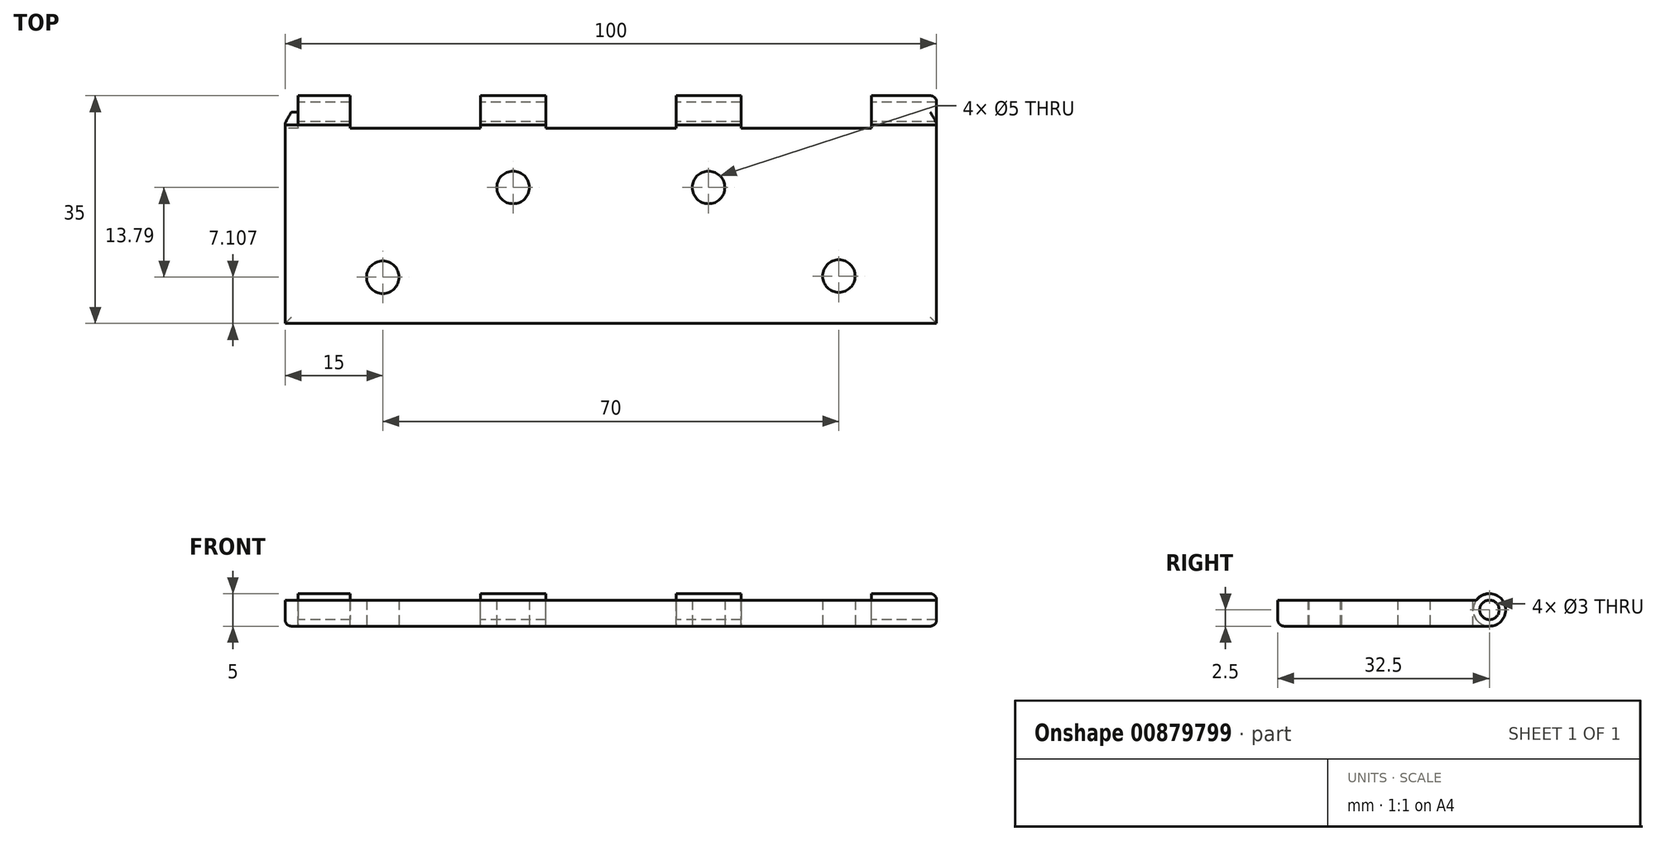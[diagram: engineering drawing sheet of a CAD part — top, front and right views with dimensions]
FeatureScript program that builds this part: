
annotation { "Feature Type Name" : "Feature", "Feature Type Description" : "" }
export const myFeature = defineFeature(function(context is Context, id is Id, definition is map)
    precondition{}
    {
        {
            var Q0;
            Q0=qCreatedBy(makeId("Top.planeOp"),FACE);
            var sketch = newSketch(context, id + "F0", { "sketchPlane" : qUnion([Q0])});
            skLineSegment(sketch, "E0.bottom", {"start": v(-50, 15) * mm, "end": v(50, 15) * mm});
            skLineSegment(sketch, "E0.top", {"start": v(-50, -15) * mm, "end": v(50, -15) * mm});
            skLineSegment(sketch, "E0.left", {"start": v(-50, 15) * mm, "end": v(-50, -15) * mm});
            skLineSegment(sketch, "E0.right", {"start": v(50, 15) * mm, "end": v(50, -15) * mm});
            skCircle(sketch, "E1", {"center": v(-35, -7.9) * mm, "radius": 2.5 * mm});
            skCircle(sketch, "E2", {"center": v(-15, 5.9) * mm, "radius": 2.5 * mm});
            skCircle(sketch, "E3", {"center": v(15, 5.9) * mm, "radius": 2.5 * mm});
            skCircle(sketch, "E4", {"center": v(35, -7.71) * mm, "radius": 2.5 * mm});
            skSolve(sketch);
        }
        {
            var Q0;
            Q0=makeQuery(id+"F0.imprint","IMPRINT",FACE,{"disambiguationData":[TD([[makeQuery(id+"F0.imprint","IMPRINT",EDGE,{"derivedFrom":sQuery(id+"F0.wireOp",EDGE,"E0.bottom")}),-1.0]])]});
            extrude(context, id + "F1", {"entities" : qUnion([Q0]), "depth" : 5 * mm, "offsetDistance" : 25 * mm});
        }
        {
            var Q0;
            Q0=makeQuery(id+"F1.opExtrude","SWEPT_FACE",FACE,{"disambiguationData":[OSD([sQuery(id+"F0.wireOp",EDGE,"E0.left")])]});
            var sketch = newSketch(context, id + "F2", { "sketchPlane" : qUnion([Q0])});
            skArc(sketch, "E5", {"start": v(-17.5, 5) * mm, "mid": v(-20, 2.5) * mm, "end": v(-17.5, 0) * mm});
            skLineSegment(sketch, "E6", {"start": v(-15, 5) * mm, "end": v(-17.5, 5) * mm});
            skLineSegment(sketch, "E7", {"start": v(-15, 0) * mm, "end": v(-17.5, 0) * mm});
            skCircle(sketch, "E8", {"center": v(-17.5, 2.5) * mm, "radius": 1.5 * mm});
            skSolve(sketch);
        }
        {
            var Q0;
            Q0=makeQuery(id+"F2.imprint","IMPRINT",FACE,{"disambiguationData":[TD([[makeQuery(id+"F2.imprint","IMPRINT",EDGE,{"derivedFrom":sQuery(id+"F2.wireOp",EDGE,"E5")}),1.0]])]});
            extrude(context, id + "F3", {"entities" : qUnion([Q0]), "operationType" : NewBodyOperationType.ADD, "oppositeDirection" : true, "depth" : 100 * mm, "offsetDistance" : 25 * mm});
        }
        {
            var Q0;
            Q0=makeQuery(id+"F3.boolean.opBoolean","MERGE",FACE,{"derivedFrom":[makeQuery(id+"F1.opExtrude","CAP_FACE",FACE,{"disambiguationData":[OSD([sQuery(id+"F0.wireOp",EDGE,"E0.bottom"),sQuery(id+"F0.wireOp",EDGE,"E0.top"),sQuery(id+"F0.wireOp",EDGE,"E0.left"),sQuery(id+"F0.wireOp",EDGE,"E0.right"),sQuery(id+"F0.wireOp",EDGE,"E1"),sQuery(id+"F0.wireOp",EDGE,"E2"),sQuery(id+"F0.wireOp",EDGE,"E3"),sQuery(id+"F0.wireOp",EDGE,"E4")])],"isStart":false}),makeQuery(id+"F3.opExtrude","SWEPT_FACE",FACE,{"disambiguationData":[OSD([sQuery(id+"F2.wireOp",EDGE,"E6")])]})]});
            var sketch = newSketch(context, id + "F4", { "sketchPlane" : qUnion([Q0])});
            skLineSegment(sketch, "E9", {"start": v(0, 0) * mm, "end": v(-50, 0) * mm, "construction": true});
            skLineSegment(sketch, "E10", {"start": v(-50, 15) * mm, "end": v(50, 15) * mm, "construction": true});
            skLineSegment(sketch, "E11.bottom", {"start": v(-50, 15) * mm, "end": v(-40, 15) * mm});
            skLineSegment(sketch, "E11.top", {"start": v(-50, 20) * mm, "end": v(-40, 20) * mm});
            skLineSegment(sketch, "E11.left", {"start": v(-50, 15) * mm, "end": v(-50, 20) * mm});
            skLineSegment(sketch, "E11.right", {"start": v(-40, 15) * mm, "end": v(-40, 20) * mm});
            skLineSegment(sketch, "E12.bottom", {"start": v(-20, 15) * mm, "end": v(-10, 15) * mm});
            skLineSegment(sketch, "E12.top", {"start": v(-20, 20) * mm, "end": v(-10, 20) * mm});
            skLineSegment(sketch, "E12.left", {"start": v(-20, 15) * mm, "end": v(-20, 20) * mm});
            skLineSegment(sketch, "E12.right", {"start": v(-10, 15) * mm, "end": v(-10, 20) * mm});
            skLineSegment(sketch, "E13.bottom", {"start": v(10, 20) * mm, "end": v(20, 20) * mm});
            skLineSegment(sketch, "E13.top", {"start": v(10, 15) * mm, "end": v(20, 15) * mm});
            skLineSegment(sketch, "E13.left", {"start": v(10, 20) * mm, "end": v(10, 15) * mm});
            skLineSegment(sketch, "E13.right", {"start": v(20, 20) * mm, "end": v(20, 15) * mm});
            skLineSegment(sketch, "E14.bottom", {"start": v(50, 15) * mm, "end": v(40, 15) * mm});
            skLineSegment(sketch, "E14.top", {"start": v(50, 20) * mm, "end": v(40, 20) * mm});
            skLineSegment(sketch, "E14.left", {"start": v(50, 15) * mm, "end": v(50, 20) * mm});
            skLineSegment(sketch, "E14.right", {"start": v(40, 15) * mm, "end": v(40, 20) * mm});
            skLineSegment(sketch, "E15.bottom", {"start": v(-40, 20) * mm, "end": v(-20, 20) * mm});
            skLineSegment(sketch, "E15.top", {"start": v(-40, 15) * mm, "end": v(-20, 15) * mm});
            skLineSegment(sketch, "E15.left", {"start": v(-40, 20) * mm, "end": v(-40, 15) * mm});
            skLineSegment(sketch, "E15.right", {"start": v(-20, 20) * mm, "end": v(-20, 15) * mm});
            skLineSegment(sketch, "E16.bottom", {"start": v(-10, 20) * mm, "end": v(10, 20) * mm});
            skLineSegment(sketch, "E16.top", {"start": v(-10, 15) * mm, "end": v(10, 15) * mm});
            skLineSegment(sketch, "E16.left", {"start": v(-10, 20) * mm, "end": v(-10, 15) * mm});
            skLineSegment(sketch, "E17.bottom", {"start": v(20, 20) * mm, "end": v(40, 20) * mm});
            skLineSegment(sketch, "E17.top", {"start": v(20, 15) * mm, "end": v(40, 15) * mm});
            skLineSegment(sketch, "E17.right", {"start": v(40, 20) * mm, "end": v(40, 15) * mm});
            skSolve(sketch);
        }
        {
            var Q0;
            Q0=makeQuery(id+"F3.boolean.opBoolean","MERGE",EDGE,{"derivedFrom":[makeQuery(id+"F1.opExtrude","CAP_EDGE",EDGE,{"disambiguationData":[OSD([sQuery(id+"F0.wireOp",EDGE,"E0.left")])],"isStart":false}),makeQuery(id+"F3.opExtrude","CAP_EDGE",EDGE,{"disambiguationData":[OSD([sQuery(id+"F2.wireOp",EDGE,"E6")])],"isStart":true})]});
            var Q1;
            Q1=makeQuery(id+"F3.boolean.opBoolean","MERGE",EDGE,{"derivedFrom":[makeQuery(id+"F1.opExtrude","CAP_EDGE",EDGE,{"disambiguationData":[OSD([sQuery(id+"F0.wireOp",EDGE,"E0.left")])],"isStart":true}),makeQuery(id+"F3.opExtrude","CAP_EDGE",EDGE,{"disambiguationData":[OSD([sQuery(id+"F2.wireOp",EDGE,"E7")])],"isStart":true})]});
            var Q2;
            Q2=makeQuery(id+"F1.opExtrude","CAP_EDGE",EDGE,{"disambiguationData":[OSD([sQuery(id+"F0.wireOp",EDGE,"E0.top")])],"isStart":true});
            var Q3;
            Q3=makeQuery(id+"F1.opExtrude","CAP_EDGE",EDGE,{"disambiguationData":[OSD([sQuery(id+"F0.wireOp",EDGE,"E0.top")])],"isStart":false});
            var Q4;
            Q4=makeQuery(id+"F3.boolean.opBoolean","MERGE",EDGE,{"derivedFrom":[makeQuery(id+"F1.opExtrude","CAP_EDGE",EDGE,{"disambiguationData":[OSD([sQuery(id+"F0.wireOp",EDGE,"E0.right")])],"isStart":false}),makeQuery(id+"F3.opExtrude","CAP_EDGE",EDGE,{"disambiguationData":[OSD([sQuery(id+"F2.wireOp",EDGE,"E6")])],"isStart":false})]});
            var Q5;
            Q5=makeQuery(id+"F3.boolean.opBoolean","MERGE",EDGE,{"derivedFrom":[makeQuery(id+"F1.opExtrude","CAP_EDGE",EDGE,{"disambiguationData":[OSD([sQuery(id+"F0.wireOp",EDGE,"E0.right")])],"isStart":true}),makeQuery(id+"F3.opExtrude","CAP_EDGE",EDGE,{"disambiguationData":[OSD([sQuery(id+"F2.wireOp",EDGE,"E7")])],"isStart":false})]});
            fillet(context, id + "F5", {"entities" : qUnion([Q0, Q1, Q2, Q3, Q4, Q5]), "radius" : 1 * mm, "tangentPropagation" : true, "allowEdgeOverflow" : false});
        }
        {
            var Q0;
            {var subQ0=sQuery(id+"F4.wireOp",EDGE,"E15.bottom");Q0=makeQuery(id+"F4.imprint","IMPRINT",FACE,{"disambiguationData":[TD([[makeQuery(id+"F4.imprint","IMPRINT",EDGE,{"derivedFrom":subQ0}),-1.0]])]});}
            var Q1;
            {var subQ0=sQuery(id+"F4.wireOp",EDGE,"E15.top");Q1=makeQuery(id+"F4.imprint","IMPRINT",FACE,{"disambiguationData":[TD([[makeQuery(id+"F4.imprint","IMPRINT",EDGE,{"derivedFrom":subQ0}),1.0]])]});}
            var Q2;
            {var subQ0=sQuery(id+"F4.wireOp",EDGE,"E16.bottom");Q2=makeQuery(id+"F4.imprint","IMPRINT",FACE,{"disambiguationData":[TD([[makeQuery(id+"F4.imprint","IMPRINT",EDGE,{"derivedFrom":subQ0}),-1.0]])]});}
            var Q3;
            {var subQ0=sQuery(id+"F4.wireOp",EDGE,"E16.top");Q3=makeQuery(id+"F4.imprint","IMPRINT",FACE,{"disambiguationData":[TD([[makeQuery(id+"F4.imprint","IMPRINT",EDGE,{"derivedFrom":subQ0}),1.0]])]});}
            var Q4;
            {var subQ0=sQuery(id+"F4.wireOp",EDGE,"E17.bottom");Q4=makeQuery(id+"F4.imprint","IMPRINT",FACE,{"disambiguationData":[TD([[makeQuery(id+"F4.imprint","IMPRINT",EDGE,{"derivedFrom":subQ0}),-1.0]])]});}
            var Q5;
            {var subQ0=sQuery(id+"F4.wireOp",EDGE,"E17.top");Q5=makeQuery(id+"F4.imprint","IMPRINT",FACE,{"disambiguationData":[TD([[makeQuery(id+"F4.imprint","IMPRINT",EDGE,{"derivedFrom":subQ0}),1.0]])]});}
            extrude(context, id + "F6", {"entities" : qUnion([Q0, Q1, Q2, Q3, Q4, Q5]), "operationType" : NewBodyOperationType.REMOVE, "oppositeDirection" : true, "depth" : 25 * mm, "offsetDistance" : 25 * mm});
        }
        {
            var Q0;
            {var subQ0=sQuery(id+"F0.wireOp",EDGE,"E0.left");Q0=makeQuery(id+"F3.boolean.opBoolean","MERGE",FACE,{"derivedFrom":[makeQuery(id+"F1.opExtrude","SWEPT_FACE",FACE,{"disambiguationData":[OSD([subQ0])]}),makeQuery(id+"F3.opExtrude","CAP_FACE",FACE,{"disambiguationData":[OSD([sQuery(id+"F0.wireOp",EDGE,"E0.bottom"),subQ0,sQuery(id+"F2.wireOp",EDGE,"E5"),sQuery(id+"F2.wireOp",EDGE,"E6"),sQuery(id+"F2.wireOp",EDGE,"E7"),sQuery(id+"F2.wireOp",EDGE,"E8")])],"isStart":true})]});}
            var sketch = newSketch(context, id + "F7", { "sketchPlane" : qUnion([Q0])});
            skCircle(sketch, "E18", {"center": v(-17.5, 2.5) * mm, "radius": 2.5 * mm});
            skLineSegment(sketch, "E19.top", {"start": v(-17.5, 0) * mm, "end": v(15, 0) * mm});
            skLineSegment(sketch, "E19.right", {"start": v(15, 1.5) * mm, "end": v(15, 0) * mm});
            skLineSegment(sketch, "E20.bottom", {"start": v(-15.2, 1.5) * mm, "end": v(15, 1.5) * mm});
            skLineSegment(sketch, "E21.top", {"start": v(-17.5, 5.25) * mm, "end": v(15, 5.25) * mm});
            skLineSegment(sketch, "E21.right", {"start": v(15, 1.5) * mm, "end": v(15, 5.25) * mm});
            skLineSegment(sketch, "E22.trimOffspring", {"start": v(-17.5, 5) * mm, "end": v(-17.5, 5.25) * mm});
            skSolve(sketch);
        }
        {
            var Q0;
            {var subQ5=sQuery(id+"F7.wireOp",EDGE,"E21.top");Q0=makeQuery(id+"F7.imprint","IMPRINT",FACE,{"disambiguationData":[TD([[makeQuery(id+"F7.imprint","IMPRINT",EDGE,{"derivedFrom":subQ5}),-1.0]])]});}
            var Q1;
            {var subQ0=sQuery(id+"F7.wireOp",EDGE,"E20.bottom");Q1=makeQuery(id+"F7.imprint","IMPRINT",FACE,{"disambiguationData":[TD([[makeQuery(id+"F7.imprint","IMPRINT",EDGE,{"derivedFrom":subQ0}),1.0]])]});}
            extrude(context, id + "F8", {"entities" : qUnion([Q0, Q1]), "operationType" : NewBodyOperationType.REMOVE, "endBound" : BoundingType.THROUGH_ALL, "oppositeDirection" : true, "depth" : 25 * mm, "offsetDistance" : 25 * mm});
        }
        {
            var Q0;
            {var subQ0=sQuery(id+"F0.wireOp",EDGE,"E0.left");Q0=makeQuery(id+"F3.boolean.opBoolean","MERGE",FACE,{"derivedFrom":[makeQuery(id+"F1.opExtrude","SWEPT_FACE",FACE,{"disambiguationData":[OSD([subQ0])]}),makeQuery(id+"F3.opExtrude","CAP_FACE",FACE,{"disambiguationData":[OSD([sQuery(id+"F0.wireOp",EDGE,"E0.bottom"),subQ0,sQuery(id+"F2.wireOp",EDGE,"E5"),sQuery(id+"F2.wireOp",EDGE,"E6"),sQuery(id+"F2.wireOp",EDGE,"E7"),sQuery(id+"F2.wireOp",EDGE,"E8")])],"isStart":true})]});}
            var sketch = newSketch(context, id + "F9", { "sketchPlane" : qUnion([Q0])});
            skCircle(sketch, "E23", {"center": v(-17.5, 2.5) * mm, "radius": 2.5 * mm});
            skSolve(sketch);
        }
        {
            var Q0;
            {var subQ1=sQuery(id+"F2.wireOp",EDGE,"E8");var subQ9=makeQuery(id+"F3.opExtrude","CAP_EDGE",EDGE,{"disambiguationData":[OSD([subQ1])],"isStart":true});Q0=makeQuery(id+"F9.imprint","IMPRINT",FACE,{"disambiguationData":[TD([[makeQuery(id+"F9.imprint","IMPRINT",EDGE,{"derivedFrom":subQ9}),1.0]])]});}
            var Q1;
            {var subQ0=sQuery(id+"F2.wireOp",EDGE,"E8");var subQ1=makeQuery(id+"F3.opExtrude","CAP_EDGE",EDGE,{"disambiguationData":[OSD([subQ0])],"isStart":true});Q1=makeQuery(id+"F9.imprint","IMPRINT",FACE,{"disambiguationData":[TD([[makeQuery(id+"F9.imprint","IMPRINT",EDGE,{"derivedFrom":subQ1}),-1.0]])]});}
            extrude(context, id + "F10", {"entities" : qUnion([Q0, Q1]), "operationType" : NewBodyOperationType.REMOVE, "oppositeDirection" : true, "depth" : 2 * mm, "offsetDistance" : 25 * mm});
        }
    });
